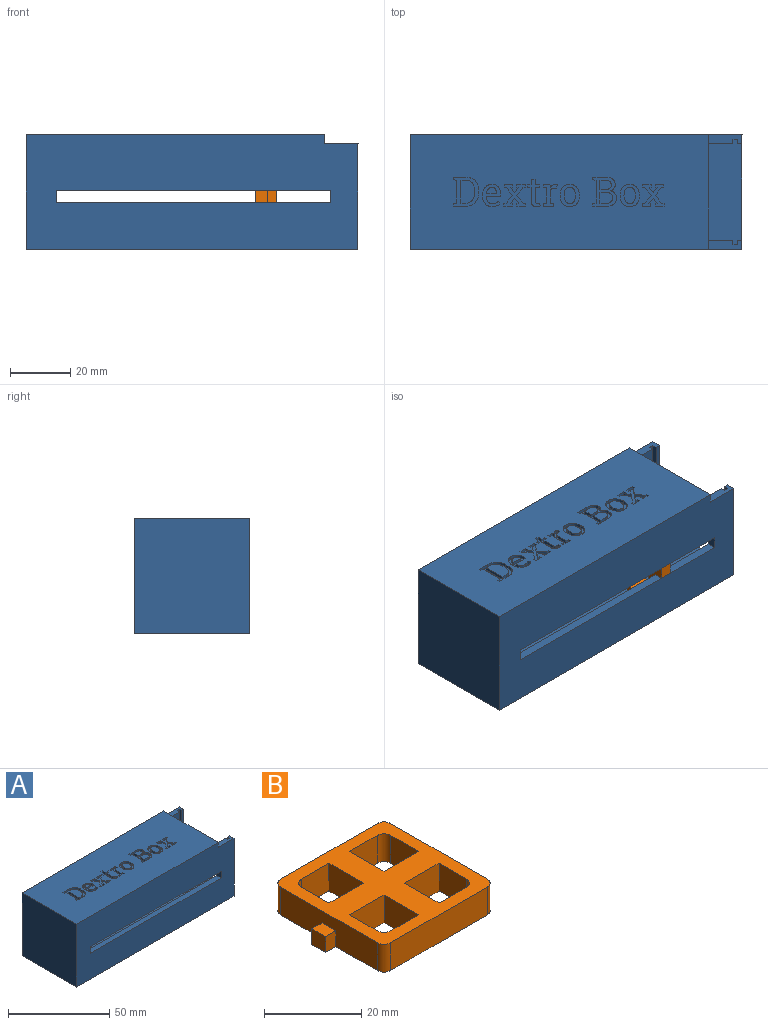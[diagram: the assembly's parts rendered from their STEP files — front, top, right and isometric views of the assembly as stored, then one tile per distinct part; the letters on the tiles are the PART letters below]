
ASSEMBLY  parts=2 mates=1
PART A: 253 faces, bbox 110x38x38 mm
  f0: plane 99x38mm, normal (0,0,1), area 3454.2mm2, adj f3,f4,f16,f18,f30,f31,f32,f33
  f1: plane 104x32mm, normal (0,1,0), area 2964mm2, adj f6,f10,f11,f19,f21,f22,f23,f24
  f2: plane 104x32mm, normal (0,-1,0), area 2964mm2, adj f5,f11,f12,f19,f21,f26,f27,f28
  f3: plane 110x38mm, normal (0,1,0), area 3783mm2, adj f0,f5,f16,f17,f18,f20,f26,f27
  f4: plane 110x38mm, normal (0,-1,0), area 3783mm2, adj f0,f6,f16,f17,f18,f20,f22,f23
  f5: plane 11x3mm, normal (0,0,1), area 30.7mm2, adj f2,f3,f12,f13,f14,f15,f17,f18
  f6: plane 11x3mm, normal (0,0,1), area 30.8mm2, adj f1,f4,f7,f8,f9,f10,f17,f18
  f7: plane 32x1.5mm, normal (0,1,0), area 48mm2, adj f6,f8,f17,f21
  f8: plane 32x1.5mm, normal (-1,0,0), area 48mm2, adj f6,f7,f9,f21
  f9: plane 32x1.5mm, normal (0,1,0), area 48mm2, adj f6,f8,f10,f21
  f10: plane 32x1.5mm, normal (1,0,0), area 48mm2, adj f1,f6,f9,f21
  f11: plane 32x32mm, normal (1,0,0), area 1024mm2, adj f1,f2,f19,f21
  f12: plane 32x1.5mm, normal (1,0,0), area 48mm2, adj f2,f5,f13,f21
  f13: plane 32x1.5mm, normal (0,-1,0), area 48mm2, adj f5,f12,f14,f21
  f14: plane 32x1.5mm, normal (-1,0,0), area 48mm2, adj f5,f13,f15,f21
  f15: plane 32x1.5mm, normal (0,-1,0), area 48mm2, adj f5,f14,f17,f21
  f16: plane 38x38mm, normal (-1,0,0), area 1444mm2, adj f0,f3,f4,f20
  f17: plane 38x35mm, normal (1,0,0), area 306mm2, adj f3,f4,f5,f6,f7,f15,f20,f21
  f18: plane 38x3mm, normal (1,0,0), area 114mm2, adj f0,f3,f4,f5,f6,f19
  f19: plane 96x32mm, normal (0,0,-1), area 3072mm2, adj f1,f2,f11,f18
  f20: plane 110x38mm, normal (0,0,-1), area 4180mm2, adj f3,f4,f16,f17
  f21: plane 107x35mm, normal (0,0,1), area 3428.5mm2, adj f1,f2,f7,f8,f9,f10,f11,f12
  f22: plane 4x3mm, normal (-1,0,0), area 12mm2, adj f1,f4,f23,f25
  f23: plane 91x3mm, normal (0,0,1), area 273mm2, adj f1,f4,f22,f24
  f24: plane 4x3mm, normal (1,0,0), area 12mm2, adj f1,f4,f23,f25
  f25: plane 91x3mm, normal (0,0,-1), area 273mm2, adj f1,f4,f22,f24
  f26: plane 91x3mm, normal (0,0,-1), area 273mm2, adj f2,f3,f27,f29
  f27: plane 4x3mm, normal (1,0,0), area 12mm2, adj f2,f3,f26,f28
  f28: plane 91x3mm, normal (0,0,1), area 273mm2, adj f2,f3,f27,f29
  f29: plane 4x3mm, normal (-1,0,0), area 12mm2, adj f2,f3,f26,f28
  f30: plane 1x0.77mm, normal (0.2,-0.98,0), area 0.8mm2, adj f0,f31,f57,f58
  f31: plane 1x0.83mm, normal (1,0,0), area 0.8mm2, adj f0,f30,f32,f58
  f32: plane 2.82x1mm, normal (0,1,0), area 2.8mm2, adj f0,f31,f33,f58
  f33: plane 1x0.83mm, normal (-1,0,0), area 0.8mm2, adj f0,f32,f34,f58
  f34: plane 1x0.64mm, normal (-0.11,-0.99,0), area 0.6mm2, adj f0,f33,f35,f58
  f35: plane 1.8x1.4mm, normal (-0.79,0.61,0), area 2.3mm2, adj f0,f34,f36,f58
  f36: plane 1.8x1.4mm, normal (0.79,0.62,0), area 2.3mm2, adj f0,f35,f37,f58
  f37: plane 1x0.64mm, normal (0.11,-0.99,0), area 0.6mm2, adj f0,f36,f38,f58
  f38: plane 1x0.83mm, normal (1,0,0), area 0.8mm2, adj f0,f37,f39,f58
  f39: plane 2.81x1mm, normal (0,1,0), area 2.8mm2, adj f0,f38,f40,f58
  f40: plane 1x0.83mm, normal (-1,0,0), area 0.8mm2, adj f0,f39,f41,f58
  f41: plane 1x0.78mm, normal (-0.19,-0.98,0), area 0.8mm2, adj f0,f40,f42,f58
  f42: plane 2.63x2.1mm, normal (-0.78,-0.62,0), area 3.4mm2, adj f0,f41,f43,f58
  f43: plane 2.55x2.04mm, normal (-0.78,0.63,0), area 3.3mm2, adj f0,f42,f44,f58
  f44: plane 1x0.77mm, normal (-0.19,0.98,0), area 0.8mm2, adj f0,f43,f45,f58
  f45: plane 1x0.84mm, normal (-1,0,0), area 0.8mm2, adj f0,f44,f46,f58
  f46: plane 2.83x1mm, normal (0,-1,0), area 2.8mm2, adj f0,f45,f47,f58
  f47: plane 1x0.84mm, normal (1,0,0), area 0.8mm2, adj f0,f46,f48,f58
  f48: plane 1x0.64mm, normal (0.11,0.99,0), area 0.6mm2, adj f0,f47,f49,f58
  f49: plane 1.73x1.34mm, normal (0.79,-0.61,0), area 2.2mm2, adj f0,f48,f50,f58
  f50: plane 1.72x1.34mm, normal (-0.79,-0.61,0), area 2.2mm2, adj f0,f49,f51,f58
  f51: plane 1x0.65mm, normal (-0.12,0.99,0), area 0.7mm2, adj f0,f50,f52,f58
  f52: plane 1x0.84mm, normal (-1,0,0), area 0.8mm2, adj f0,f51,f53,f58
  f53: plane 2.81x1mm, normal (0,-1,0), area 2.8mm2, adj f0,f52,f54,f58
  f54: plane 1x0.84mm, normal (1,0,0), area 0.8mm2, adj f0,f53,f55,f58
  f55: plane 1x0.77mm, normal (0.19,0.98,0), area 0.8mm2, adj f0,f54,f56,f58
  f56: plane 2.55x2.04mm, normal (0.78,0.63,0), area 3.3mm2, adj f0,f55,f57,f58
  f57: plane 2.63x2.11mm, normal (0.78,-0.63,0), area 3.4mm2, adj f0,f30,f56,f58
  f58: plane 7.16x7.15mm, normal (0,0,1), area 24.2mm2, adj f30,f31,f32,f33,f34,f35,f36,f37
  f59: plane 2.18x1mm, normal (0,-1,0), area 2.2mm2, adj f60,f87,f88,f248
  f60: plane 3.07x1mm, normal (-1,0,0), area 3.1mm2, adj f59,f61,f88,f248
  f61: plane 1.84x1mm, normal (0,1,0), area 1.8mm2, adj f60,f62,f88,f248
  f62: extruded ~1.42x1mm, area 1.5mm2, adj f61,f63,f88,f248
  f63: extruded ~1.17x1mm, area 1.3mm2, adj f62,f64,f88,f248
  f64: extruded ~1.1x1mm, area 1.2mm2, adj f63,f87,f88,f248
  f65: plane 3.5x1mm, normal (-1,0,0), area 3.5mm2, adj f66,f85,f88,f89
  f66: plane 2.45x1mm, normal (0,1,0), area 2.4mm2, adj f65,f67,f88,f89
  f67: extruded ~1.27x1mm, area 1.4mm2, adj f66,f68,f88,f89
  f68: extruded ~1.33x1mm, area 1.4mm2, adj f67,f69,f88,f89
  f69: extruded ~1.25x1mm, area 1.4mm2, adj f68,f70,f88,f89
  f70: extruded ~1.39x1mm, area 1.5mm2, adj f69,f85,f88,f89
  f71: extruded ~2.36x1mm, area 2.5mm2, adj f0,f72,f86,f88
  f72: plane 4.22x1mm, normal (0,-1,0), area 4.2mm2, adj f0,f71,f73,f88
  f73: plane 1x0.84mm, normal (1,0,0), area 0.8mm2, adj f0,f72,f74,f88
  f74: plane 1.08x1mm, normal (0.17,0.99,0), area 1.1mm2, adj f0,f73,f75,f88
  f75: plane 7.59x1mm, normal (1,0,0), area 7.6mm2, adj f0,f74,f76,f88
  f76: plane 1.08x1mm, normal (0.17,-0.99,0), area 1.1mm2, adj f0,f75,f77,f88
  f77: plane 1x0.83mm, normal (1,0,0), area 0.8mm2, adj f0,f76,f78,f88
  f78: plane 4.63x1mm, normal (0,1,0), area 4.6mm2, adj f0,f77,f79,f88
  f79: extruded ~2.33x1mm, area 2.5mm2, adj f0,f78,f80,f88
  f80: extruded ~2.02x1mm, area 2.3mm2, adj f0,f79,f81,f88
  f81: extruded ~1.56x1mm, area 1.7mm2, adj f0,f80,f82,f88
  f82: extruded ~1.37x1mm, area 1.7mm2, adj f0,f81,f83,f88
  f83: extruded ~1.08x1mm, area 1.3mm2, adj f0,f82,f84,f88
  f84: extruded ~1.15x1mm, area 1.2mm2, adj f0,f83,f86,f88
  f85: plane 2.25x1mm, normal (0,-1,0), area 2.2mm2, adj f65,f70,f88,f89
  f86: extruded ~1.95x1mm, area 2.2mm2, adj f0,f71,f84,f88
  f87: extruded ~1.13x1mm, area 1.2mm2, adj f59,f64,f88,f248
  f88: plane 9.63x7.82mm, normal (0,0,1), area 36.4mm2, adj f59,f60,f61,f62,f63,f64,f65,f66
  f89: plane 4.13x3.5mm, normal (0,0,1), area 13.4mm2, adj f65,f66,f67,f68,f69,f70,f85
  f90: extruded ~1.88x1mm, area 2mm2, adj f91,f109,f110,f249
  f91: plane 1x0.15mm, normal (-1,0,0), area 0.1mm2, adj f90,f92,f110,f249
  f92: extruded ~1.87x1mm, area 2mm2, adj f91,f93,f110,f249
  f93: extruded ~1.42x1mm, area 1.7mm2, adj f92,f94,f110,f249
  f94: extruded ~1.42x1mm, area 1.7mm2, adj f93,f95,f110,f249
  f95: extruded ~1.87x1mm, area 2mm2, adj f94,f96,f110,f249
  f96: plane 1x0.15mm, normal (1,0,0), area 0.1mm2, adj f95,f97,f110,f249
  f97: extruded ~1.88x1mm, area 2mm2, adj f96,f98,f110,f249
  f98: extruded ~1.41x1mm, area 1.7mm2, adj f97,f109,f110,f249
  f99: extruded ~2.62x1mm, area 2.8mm2, adj f0,f100,f108,f110
  f100: plane 1x0.15mm, normal (1,0,0), area 0.1mm2, adj f0,f99,f101,f110
  f101: extruded ~2.62x1mm, area 2.8mm2, adj f0,f100,f102,f110
  f102: extruded ~2.35x1.02mm, area 2.7mm2, adj f0,f101,f103,f110
  f103: extruded ~2.34x1.02mm, area 2.6mm2, adj f0,f102,f104,f110
  f104: extruded ~2.62x1mm, area 2.8mm2, adj f0,f103,f105,f110
  f105: plane 1x0.15mm, normal (-1,0,0), area 0.1mm2, adj f0,f104,f106,f110
  f106: extruded ~2.62x1mm, area 2.8mm2, adj f0,f105,f107,f110
  f107: extruded ~2.34x1.03mm, area 2.6mm2, adj f0,f106,f108,f110
  f108: extruded ~2.34x1.03mm, area 2.6mm2, adj f0,f99,f107,f110
  f109: extruded ~1.43x1mm, area 1.7mm2, adj f90,f98,f110,f249
  f110: plane 7.43x6.4mm, normal (0,0,1), area 21.9mm2, adj f90,f91,f92,f93,f94,f95,f96,f97
  f111: extruded ~1.88x1mm, area 2mm2, adj f112,f130,f131,f250
  f112: plane 1x0.15mm, normal (-1,0,0), area 0.1mm2, adj f111,f113,f131,f250
  f113: extruded ~1.87x1mm, area 2mm2, adj f112,f114,f131,f250
  f114: extruded ~1.42x1mm, area 1.7mm2, adj f113,f115,f131,f250
  f115: extruded ~1.42x1mm, area 1.7mm2, adj f114,f116,f131,f250
  f116: extruded ~1.87x1mm, area 2mm2, adj f115,f117,f131,f250
  f117: plane 1x0.15mm, normal (1,0,0), area 0.1mm2, adj f116,f118,f131,f250
  f118: extruded ~1.88x1mm, area 2mm2, adj f117,f119,f131,f250
  f119: extruded ~1.41x1mm, area 1.7mm2, adj f118,f130,f131,f250
  f120: extruded ~2.62x1mm, area 2.8mm2, adj f0,f121,f129,f131
  f121: plane 1x0.15mm, normal (1,0,0), area 0.1mm2, adj f0,f120,f122,f131
  f122: extruded ~2.62x1mm, area 2.8mm2, adj f0,f121,f123,f131
  f123: extruded ~2.35x1.02mm, area 2.7mm2, adj f0,f122,f124,f131
  f124: extruded ~2.34x1.02mm, area 2.6mm2, adj f0,f123,f125,f131
  f125: extruded ~2.62x1mm, area 2.8mm2, adj f0,f124,f126,f131
  f126: plane 1x0.15mm, normal (-1,0,0), area 0.1mm2, adj f0,f125,f127,f131
  f127: extruded ~2.62x1mm, area 2.8mm2, adj f0,f126,f128,f131
  f128: extruded ~2.34x1.03mm, area 2.6mm2, adj f0,f127,f129,f131
  f129: extruded ~2.34x1.03mm, area 2.6mm2, adj f0,f120,f128,f131
  f130: extruded ~1.43x1mm, area 1.7mm2, adj f111,f119,f131,f250
  f131: plane 7.43x6.4mm, normal (0,0,1), area 21.9mm2, adj f111,f112,f113,f114,f115,f116,f117,f118
  f132: extruded ~1.12x1mm, area 1.3mm2, adj f133,f155,f156,f251
  f133: extruded ~1.22x1mm, area 1.4mm2, adj f132,f134,f156,f251
  f134: extruded ~1.28x1mm, area 1.4mm2, adj f133,f135,f156,f251
  f135: plane 1x0.17mm, normal (1,0,0), area 0.2mm2, adj f134,f136,f156,f251
  f136: plane 3.3x1mm, normal (0,-1,0), area 3.3mm2, adj f135,f137,f156,f251
  f137: plane 1x0.03mm, normal (-0.92,-0.4,0), area 0mm2, adj f136,f155,f156,f251
  f138: extruded ~2.38x1mm, area 2.7mm2, adj f0,f139,f154,f156
  f139: extruded ~1.52x1mm, area 1.5mm2, adj f0,f138,f140,f156
  f140: extruded ~1.02x1mm, area 1.2mm2, adj f0,f139,f141,f156
  f141: plane 1x0.85mm, normal (-0.86,-0.52,0), area 1mm2, adj f0,f140,f142,f156
  f142: extruded ~1x0.86mm, area 1mm2, adj f0,f141,f143,f156
  f143: extruded ~1.16x1mm, area 1.2mm2, adj f0,f142,f144,f156
  f144: extruded ~1.41x1mm, area 1.6mm2, adj f0,f143,f145,f156
  f145: extruded ~1.7x1mm, area 1.8mm2, adj f0,f144,f146,f156
  f146: plane 1x0.03mm, normal (-0.85,0.53,0), area 0mm2, adj f0,f145,f147,f156
  f147: plane 4.65x1mm, normal (0,1,0), area 4.6mm2, adj f0,f146,f148,f156
  f148: plane 1x0.81mm, normal (-1,0,0), area 0.8mm2, adj f0,f147,f149,f156
  f149: extruded ~2.33x1mm, area 2.5mm2, adj f0,f148,f150,f156
  f150: extruded ~2.19x1mm, area 2.4mm2, adj f0,f149,f151,f156
  f151: extruded ~2.15x1.02mm, area 2.5mm2, adj f0,f150,f152,f156
  f152: extruded ~2.54x1mm, area 2.8mm2, adj f0,f151,f153,f156
  f153: plane 1x0.29mm, normal (1,0,0), area 0.3mm2, adj f0,f152,f154,f156
  f154: extruded ~2.58x1mm, area 2.8mm2, adj f0,f138,f153,f156
  f155: extruded ~1.39x1mm, area 1.5mm2, adj f132,f137,f156,f251
  f156: plane 7.43x6mm, normal (0,0,1), area 22.6mm2, adj f132,f133,f134,f135,f136,f137,f138,f139
  f157: plane 1.73x1mm, normal (-1,0,0), area 1.7mm2, adj f0,f158,f176,f177
  f158: plane 1.3x1mm, normal (0,-1,0), area 1.3mm2, adj f0,f157,f159,f177
  f159: plane 1.73x1mm, normal (1,0,0), area 1.7mm2, adj f0,f158,f160,f177
  f160: plane 1.13x1mm, normal (0,-1,0), area 1.1mm2, adj f0,f159,f161,f177
  f161: plane 1x0.97mm, normal (1,0,0), area 1mm2, adj f0,f160,f162,f177
  f162: plane 1.13x1mm, normal (0,1,0), area 1.1mm2, adj f0,f161,f163,f177
  f163: plane 4.35x1mm, normal (1,0,0), area 4.3mm2, adj f0,f162,f164,f177
  f164: extruded ~1.51x1mm, area 1.6mm2, adj f0,f163,f165,f177
  f165: extruded ~1.26x1mm, area 1.4mm2, adj f0,f164,f166,f177
  f166: extruded ~1x0.72mm, area 0.7mm2, adj f0,f165,f167,f177
  f167: extruded ~1x0.54mm, area 0.6mm2, adj f0,f166,f168,f177
  f168: plane 1x0.89mm, normal (-0.98,-0.2,0), area 0.9mm2, adj f0,f167,f169,f177
  f169: extruded ~1x0.36mm, area 0.4mm2, adj f0,f168,f170,f177
  f170: extruded ~1x0.39mm, area 0.4mm2, adj f0,f169,f171,f177
  f171: extruded ~1x0.55mm, area 0.6mm2, adj f0,f170,f172,f177
  f172: extruded ~1x0.71mm, area 0.8mm2, adj f0,f171,f173,f177
  f173: plane 4.35x1mm, normal (-1,0,0), area 4.3mm2, adj f0,f172,f174,f177
  f174: plane 1.36x1mm, normal (0,1,0), area 1.4mm2, adj f0,f173,f175,f177
  f175: plane 1x0.97mm, normal (-1,0,0), area 1mm2, adj f0,f174,f176,f177
  f176: plane 1.36x1mm, normal (0,-1,0), area 1.4mm2, adj f0,f157,f175,f177
  f177: plane 9.03x4.12mm, normal (0,0,1), area 15.3mm2, adj f157,f158,f159,f160,f161,f162,f163,f164
  f178: plane 1x0.84mm, normal (1,0,0), area 0.8mm2, adj f0,f179,f196,f197
  f179: plane 1.08x1mm, normal (0.17,0.99,0), area 1.1mm2, adj f0,f178,f180,f197
  f180: plane 5.12x1mm, normal (1,0,0), area 5.1mm2, adj f0,f179,f181,f197
  f181: plane 1.08x1mm, normal (0.17,-0.99,0), area 1.1mm2, adj f0,f180,f182,f197
  f182: plane 1x0.83mm, normal (1,0,0), area 0.8mm2, adj f0,f181,f183,f197
  f183: plane 3.46x1mm, normal (0,1,0), area 3.5mm2, adj f0,f182,f184,f197
  f184: plane 1x0.83mm, normal (-1,0,0), area 0.8mm2, adj f0,f183,f185,f197
  f185: plane 1.08x1mm, normal (-0.17,-0.99,0), area 1.1mm2, adj f0,f184,f186,f197
  f186: plane 4.11x1mm, normal (-1,0,0), area 4.1mm2, adj f0,f185,f187,f197
  f187: extruded ~1x0.68mm, area 0.9mm2, adj f0,f186,f188,f197
  f188: extruded ~1x0.87mm, area 0.9mm2, adj f0,f187,f189,f197
  f189: plane 1x0.74mm, normal (0.05,1,0), area 0.7mm2, adj f0,f188,f190,f197
  f190: plane 1.21x1mm, normal (-0.99,0.14,0), area 1.2mm2, adj f0,f189,f191,f197
  f191: extruded ~1x0.25mm, area 0.3mm2, adj f0,f190,f192,f197
  f192: extruded ~1x0.31mm, area 0.3mm2, adj f0,f191,f193,f197
  f193: extruded ~1.02x1mm, area 1.1mm2, adj f0,f192,f194,f197
  f194: extruded ~1x0.86mm, area 1.2mm2, adj f0,f193,f195,f197
  f195: plane 1.04x1mm, normal (-0.99,-0.12,0), area 1mm2, adj f0,f194,f196,f197
  f196: plane 2.24x1mm, normal (0,-1,0), area 2.2mm2, adj f0,f178,f195,f197
  f197: plane 7.29x4.7mm, normal (0,0,1), area 14.8mm2, adj f178,f179,f180,f181,f182,f183,f184,f185
  f198: plane 1x0.77mm, normal (0.2,-0.98,0), area 0.8mm2, adj f0,f199,f225,f226
  f199: plane 1x0.83mm, normal (1,0,0), area 0.8mm2, adj f0,f198,f200,f226
  f200: plane 2.82x1mm, normal (0,1,0), area 2.8mm2, adj f0,f199,f201,f226
  f201: plane 1x0.83mm, normal (-1,0,0), area 0.8mm2, adj f0,f200,f202,f226
  f202: plane 1x0.64mm, normal (-0.11,-0.99,0), area 0.6mm2, adj f0,f201,f203,f226
  f203: plane 1.8x1.4mm, normal (-0.79,0.61,0), area 2.3mm2, adj f0,f202,f204,f226
  f204: plane 1.8x1.4mm, normal (0.79,0.62,0), area 2.3mm2, adj f0,f203,f205,f226
  f205: plane 1x0.64mm, normal (0.11,-0.99,0), area 0.6mm2, adj f0,f204,f206,f226
  f206: plane 1x0.83mm, normal (1,0,0), area 0.8mm2, adj f0,f205,f207,f226
  f207: plane 2.81x1mm, normal (0,1,0), area 2.8mm2, adj f0,f206,f208,f226
  f208: plane 1x0.83mm, normal (-1,0,0), area 0.8mm2, adj f0,f207,f209,f226
  f209: plane 1x0.78mm, normal (-0.19,-0.98,0), area 0.8mm2, adj f0,f208,f210,f226
  f210: plane 2.63x2.1mm, normal (-0.78,-0.62,0), area 3.4mm2, adj f0,f209,f211,f226
  f211: plane 2.55x2.04mm, normal (-0.78,0.63,0), area 3.3mm2, adj f0,f210,f212,f226
  f212: plane 1x0.77mm, normal (-0.19,0.98,0), area 0.8mm2, adj f0,f211,f213,f226
  f213: plane 1x0.84mm, normal (-1,0,0), area 0.8mm2, adj f0,f212,f214,f226
  f214: plane 2.83x1mm, normal (0,-1,0), area 2.8mm2, adj f0,f213,f215,f226
  f215: plane 1x0.84mm, normal (1,0,0), area 0.8mm2, adj f0,f214,f216,f226
  f216: plane 1x0.64mm, normal (0.11,0.99,0), area 0.6mm2, adj f0,f215,f217,f226
  f217: plane 1.73x1.34mm, normal (0.79,-0.61,0), area 2.2mm2, adj f0,f216,f218,f226
  f218: plane 1.72x1.34mm, normal (-0.79,-0.61,0), area 2.2mm2, adj f0,f217,f219,f226
  f219: plane 1x0.65mm, normal (-0.12,0.99,0), area 0.7mm2, adj f0,f218,f220,f226
  f220: plane 1x0.84mm, normal (-1,0,0), area 0.8mm2, adj f0,f219,f221,f226
  f221: plane 2.81x1mm, normal (0,-1,0), area 2.8mm2, adj f0,f220,f222,f226
  f222: plane 1x0.84mm, normal (1,0,0), area 0.8mm2, adj f0,f221,f223,f226
  f223: plane 1x0.77mm, normal (0.19,0.98,0), area 0.8mm2, adj f0,f222,f224,f226
  f224: plane 2.55x2.04mm, normal (0.78,0.63,0), area 3.3mm2, adj f0,f223,f225,f226
  f225: plane 2.63x2.11mm, normal (0.78,-0.63,0), area 3.4mm2, adj f0,f198,f224,f226
  f226: plane 7.16x7.15mm, normal (0,0,1), area 24.2mm2, adj f198,f199,f200,f201,f202,f203,f204,f205
  f227: plane 7.59x1mm, normal (-1,0,0), area 7.6mm2, adj f228,f246,f247,f252
  f228: plane 1.65x1mm, normal (0,1,0), area 1.7mm2, adj f227,f229,f247,f252
  f229: extruded ~2.11x1mm, area 2.4mm2, adj f228,f230,f247,f252
  f230: extruded ~2.24x1mm, area 2.4mm2, adj f229,f231,f247,f252
  f231: plane 1.33x1mm, normal (1,0,0), area 1.3mm2, adj f230,f232,f247,f252
  f232: extruded ~2.26x1mm, area 2.4mm2, adj f231,f233,f247,f252
  f233: extruded ~2.11x1mm, area 2.4mm2, adj f232,f246,f247,f252
  f234: extruded ~3.03x1.16mm, area 3.3mm2, adj f0,f235,f245,f247
  f235: plane 4.04x1mm, normal (0,-1,0), area 4mm2, adj f0,f234,f236,f247
  f236: plane 1x0.84mm, normal (1,0,0), area 0.8mm2, adj f0,f235,f237,f247
  f237: plane 1.08x1mm, normal (0.17,0.99,0), area 1.1mm2, adj f0,f236,f238,f247
  f238: plane 7.59x1mm, normal (1,0,0), area 7.6mm2, adj f0,f237,f239,f247
  f239: plane 1.08x1mm, normal (0.17,-0.99,0), area 1.1mm2, adj f0,f238,f240,f247
  f240: plane 1x0.83mm, normal (1,0,0), area 0.8mm2, adj f0,f239,f241,f247
  f241: plane 4.04x1mm, normal (0,1,0), area 4mm2, adj f0,f240,f242,f247
  f242: extruded ~3.03x1.16mm, area 3.3mm2, adj f0,f241,f243,f247
  f243: extruded ~3x1.15mm, area 3.3mm2, adj f0,f242,f244,f247
  f244: plane 1.31x1mm, normal (-1,0,0), area 1.3mm2, adj f0,f243,f245,f247
  f245: extruded ~3x1.15mm, area 3.3mm2, adj f0,f234,f244,f247
  f246: plane 1.65x1mm, normal (0,-1,0), area 1.7mm2, adj f227,f233,f247,f252
  f247: plane 9.63x8.22mm, normal (0,0,1), area 33.1mm2, adj f227,f228,f229,f230,f231,f232,f233,f234
  f248: plane 3.75x3.07mm, normal (0,0,1), area 10.5mm2, adj f59,f60,f61,f62,f63,f64,f87
  f249: plane 5.38x3.8mm, normal (0,0,1), area 16.8mm2, adj f90,f91,f92,f93,f94,f95,f96,f97
  f250: plane 5.38x3.8mm, normal (0,0,1), area 16.8mm2, adj f111,f112,f113,f114,f115,f116,f117,f118
  f251: plane 3.32x1.97mm, normal (0,0,1), area 5.2mm2, adj f132,f133,f134,f135,f136,f137,f155
  f252: plane 7.59x4.53mm, normal (0,0,1), area 30.9mm2, adj f227,f228,f229,f230,f231,f232,f233,f246
PART B: 38 faces, bbox 38x32x7 mm
  f0: plane 28x7mm, normal (1,0,0), area 180mm2, adj f18,f23,f28,f29,f34,f36,f37
  f1: plane 28x7mm, normal (-1,0,0), area 180mm2, adj f20,f21,f28,f29,f30,f32,f33
  f2: plane 10x7mm, normal (-1,0,0), area 70mm2, adj f3,f27,f28,f29
  f3: plane 8x7mm, normal (0,1,0), area 56mm2, adj f2,f4,f28,f29
  f4: cylinder r=2mm len=7mm, axis (0,0,-1), area 22mm2, adj f3,f5,f28,f29
  f5: plane 8x7mm, normal (1,0,0), area 56mm2, adj f4,f27,f28,f29
  f6: cylinder r=2mm len=7mm, axis (0,0,-1), area 22mm2, adj f7,f24,f28,f29
  f7: plane 8x7mm, normal (0,1,0), area 56mm2, adj f6,f8,f28,f29
  f8: plane 10x7mm, normal (1,0,0), area 70mm2, adj f7,f9,f28,f29
  f9: plane 10x7mm, normal (0,-1,0), area 70mm2, adj f8,f24,f28,f29
  f10: plane 8x7mm, normal (0,-1,0), area 56mm2, adj f11,f25,f28,f29
  f11: cylinder r=2mm len=7mm, axis (0,0,-1), area 22mm2, adj f10,f12,f28,f29
  f12: plane 8x7mm, normal (-1,0,0), area 56mm2, adj f11,f13,f28,f29
  f13: plane 10x7mm, normal (0,1,0), area 70mm2, adj f12,f25,f28,f29
  f14: plane 8x7mm, normal (0,-1,0), area 56mm2, adj f15,f26,f28,f29
  f15: plane 10x7mm, normal (-1,0,0), area 70mm2, adj f14,f16,f28,f29
  f16: plane 10x7mm, normal (0,1,0), area 70mm2, adj f15,f17,f28,f29
  f17: plane 8x7mm, normal (1,0,0), area 56mm2, adj f16,f26,f28,f29
  f18: cylinder r=2mm len=7mm, axis (0,0,-1), area 22mm2, adj f0,f19,f28,f29
  f19: plane 28x7mm, normal (0,1,0), area 196mm2, adj f18,f20,f28,f29
  f20: cylinder r=2mm len=7mm, axis (0,0,-1), area 22mm2, adj f1,f19,f28,f29
  f21: cylinder r=2mm len=7mm, axis (0,0,-1), area 22mm2, adj f1,f22,f28,f29
  f22: plane 28x7mm, normal (0,-1,0), area 196mm2, adj f21,f23,f28,f29
  f23: cylinder r=2mm len=7mm, axis (0,0,-1), area 22mm2, adj f0,f22,f28,f29
  f24: plane 8x7mm, normal (-1,0,0), area 56mm2, adj f6,f9,f28,f29
  f25: plane 10x7mm, normal (1,0,0), area 70mm2, adj f10,f13,f28,f29
  f26: cylinder r=2mm len=7mm, axis (0,0,-1), area 22mm2, adj f14,f17,f28,f29
  f27: plane 10x7mm, normal (0,-1,0), area 70mm2, adj f2,f5,f28,f29
  f28: plane 32x32mm, normal (0,0,1), area 624mm2, adj f0,f1,f2,f3,f4,f5,f6,f7
  f29: plane 38x32mm, normal (0,0,-1), area 648mm2, adj f0,f1,f2,f3,f4,f5,f6,f7
  f30: plane 4x3mm, normal (0,1,0), area 12mm2, adj f1,f29,f31,f33
  f31: plane 4x4mm, normal (-1,0,0), area 16mm2, adj f29,f30,f32,f33
  f32: plane 4x3mm, normal (0,-1,0), area 12mm2, adj f1,f29,f31,f33
  f33: plane 4x3mm, normal (0,0,1), area 12mm2, adj f1,f30,f31,f32
  f34: plane 4x3mm, normal (0,-1,0), area 12mm2, adj f0,f29,f35,f37
  f35: plane 4x4mm, normal (1,0,0), area 16mm2, adj f29,f34,f36,f37
  f36: plane 4x3mm, normal (0,1,0), area 12mm2, adj f0,f29,f35,f37
  f37: plane 4x3mm, normal (0,0,1), area 12mm2, adj f0,f34,f35,f36
PLACE A t=(-34.31,24.44,4.91)mm fixed
PLACE B rot(axis=(0.58,0.58,0.58),120deg) t=(-8.52,22.08,15.24)mm
MATE slider B.f37 <-> A.f29  axis (1,0,0) through (-4.52,42.55,19.41)mm
